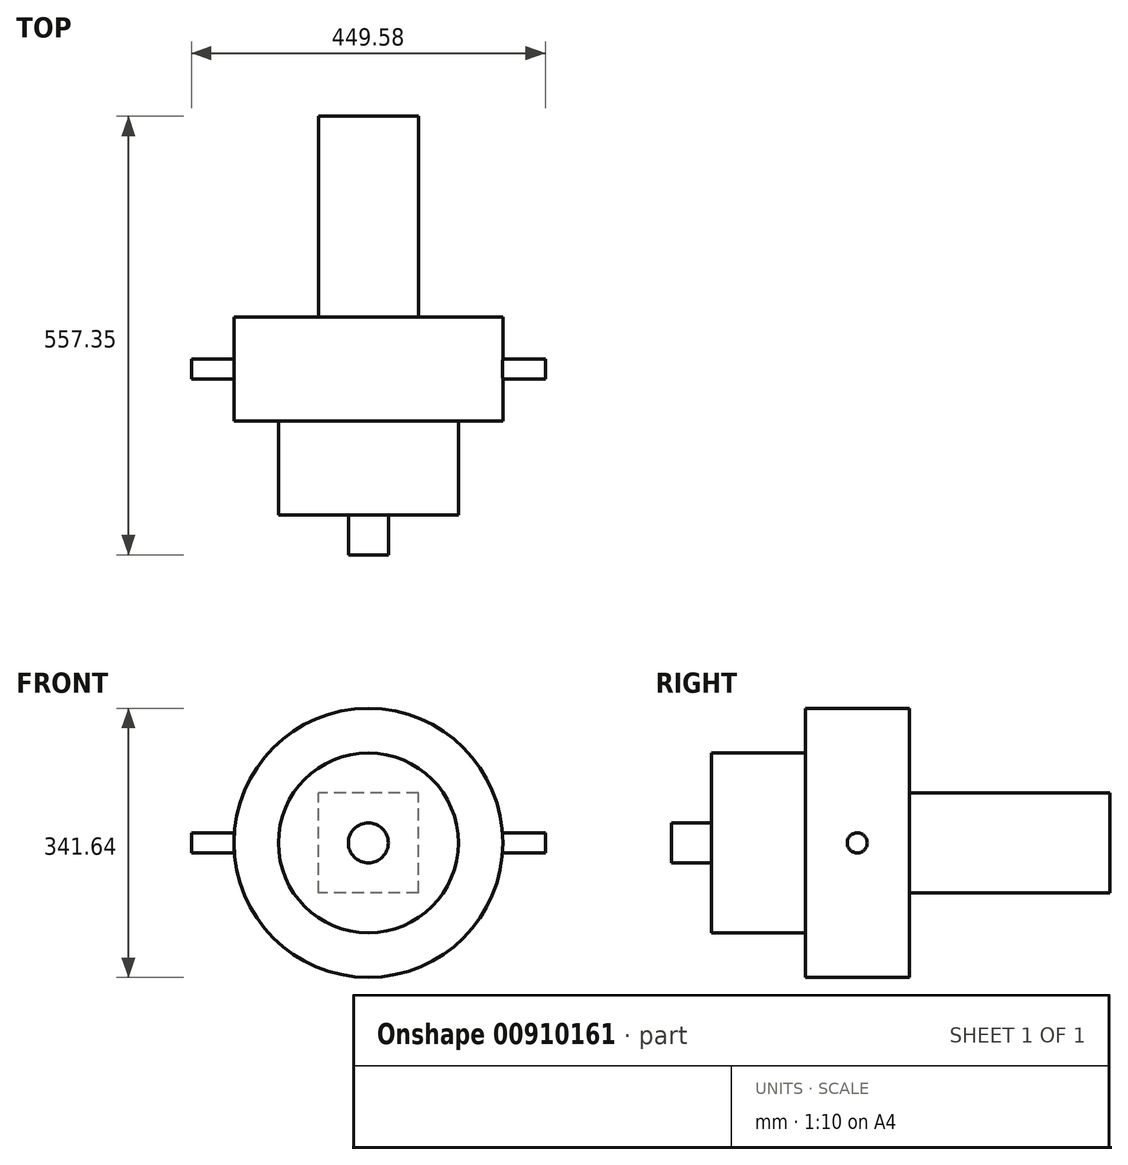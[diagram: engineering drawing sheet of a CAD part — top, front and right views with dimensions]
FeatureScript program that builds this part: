
annotation { "Feature Type Name" : "Feature", "Feature Type Description" : "" }
export const myFeature = defineFeature(function(context is Context, id is Id, definition is map)
    precondition{}
    {
        {
            var Q0;
            Q0=qCreatedBy(makeId("Front.planeOp"),FACE);
            var sketch = newSketch(context, id + "F0", { "sketchPlane" : qUnion([Q0])});
            skLineSegment(sketch, "E0.bottom", {"start": v(-63.5, 63.5) * mm, "end": v(63.5, 63.5) * mm});
            skLineSegment(sketch, "E0.top", {"start": v(-63.5, -63.5) * mm, "end": v(63.5, -63.5) * mm});
            skLineSegment(sketch, "E0.left", {"start": v(-63.5, 63.5) * mm, "end": v(-63.5, -63.5) * mm});
            skLineSegment(sketch, "E0.right", {"start": v(63.5, 63.5) * mm, "end": v(63.5, -63.5) * mm});
            skPoint(sketch, "E0.middle", {"position": v(0, 0) * mm});
            skSolve(sketch);
        }
        {
            var Q0;
            Q0=makeQuery(id+"F0.imprint","IMPRINT",FACE,{"disambiguationData":[TD([[makeQuery(id+"F0.imprint","IMPRINT",EDGE,{"derivedFrom":sQuery(id+"F0.wireOp",EDGE,"E0.bottom")}),-1.0]])]});
            extrude(context, id + "F1", {"entities" : qUnion([Q0]), "oppositeDirection" : true, "depth" : 321.13 * mm, "offsetDistance" : 25.4 * mm});
        }
        {
            var Q0;
            Q0=qCreatedBy(makeId("Front.planeOp"),FACE);
            var sketch = newSketch(context, id + "F2", { "sketchPlane" : qUnion([Q0])});
            skCircle(sketch, "E1", {"center": v(0, 0) * mm, "radius": 170.81 * mm});
            skSolve(sketch);
        }
        {
            var Q0;
            Q0 = qSketchRegion(id + "F2", true);
            extrude(context, id + "F3", {"entities" : qUnion([Q0]), "operationType" : NewBodyOperationType.ADD, "endBound" : BoundingType.SYMMETRIC, "depth" : 132.08 * mm, "offsetDistance" : 25.4 * mm});
        }
        {
            var Q0;
            Q0=makeQuery(id+"F3.opExtrude","CAP_FACE",FACE,{"disambiguationData":[OSD([sQuery(id+"F2.wireOp",EDGE,"E1")])],"isStart":false});
            var sketch = newSketch(context, id + "F4", { "sketchPlane" : qUnion([Q0])});
            skCircle(sketch, "E2", {"center": v(0, 0) * mm, "radius": 114.3 * mm});
            skSolve(sketch);
        }
        {
            var Q0;
            Q0 = qSketchRegion(id + "F4", true);
            extrude(context, id + "F5", {"entities" : qUnion([Q0]), "operationType" : NewBodyOperationType.ADD, "depth" : 119.38 * mm, "offsetDistance" : 25.4 * mm});
        }
        {
            var Q0;
            Q0=makeQuery(id+"F5.opExtrude","CAP_FACE",FACE,{"disambiguationData":[OSD([sQuery(id+"F4.wireOp",EDGE,"E2")])],"isStart":false});
            var sketch = newSketch(context, id + "F6", { "sketchPlane" : qUnion([Q0])});
            skCircle(sketch, "E3", {"center": v(0, 0) * mm, "radius": 25.4 * mm});
            skSolve(sketch);
        }
        {
            var Q0;
            Q0 = qSketchRegion(id + "F6", true);
            extrude(context, id + "F7", {"entities" : qUnion([Q0]), "operationType" : NewBodyOperationType.ADD, "depth" : 50.8 * mm, "offsetDistance" : 25.4 * mm});
        }
        {
            var Q0;
            Q0=qCreatedBy(makeId("Right.planeOp"),FACE);
            var sketch = newSketch(context, id + "F8", { "sketchPlane" : qUnion([Q0])});
            skCircle(sketch, "E4", {"center": v(0, 0) * mm, "radius": 12.7 * mm});
            skSolve(sketch);
        }
        {
            var Q0;
            Q0 = qSketchRegion(id + "F8", true);
            extrude(context, id + "F9", {"entities" : qUnion([Q0]), "operationType" : NewBodyOperationType.ADD, "endBound" : BoundingType.SYMMETRIC, "depth" : 449.58 * mm, "offsetDistance" : 25.4 * mm});
        }
    });
